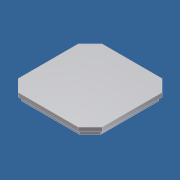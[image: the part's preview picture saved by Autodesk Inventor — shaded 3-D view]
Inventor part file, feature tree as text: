
AUTODESK INVENTOR PART (.ipt)
format: ipt  version: unknown  size: 200,192 bytes
history: native  units: mm
features: extrude x2, sketch x2
ambient origin geometry x8: Origin, YZ Plane, XZ Plane, XY Plane, X Axis, Y Axis, Z Axis, Center Point
feature tree (4):
  extrude  "Estrusione10"  Depth=59.0mm
  extrude  "Estrusione11"  Depth=59.0mm
  sketch  "Schizzo1"
  sketch  "Schizzo12"
